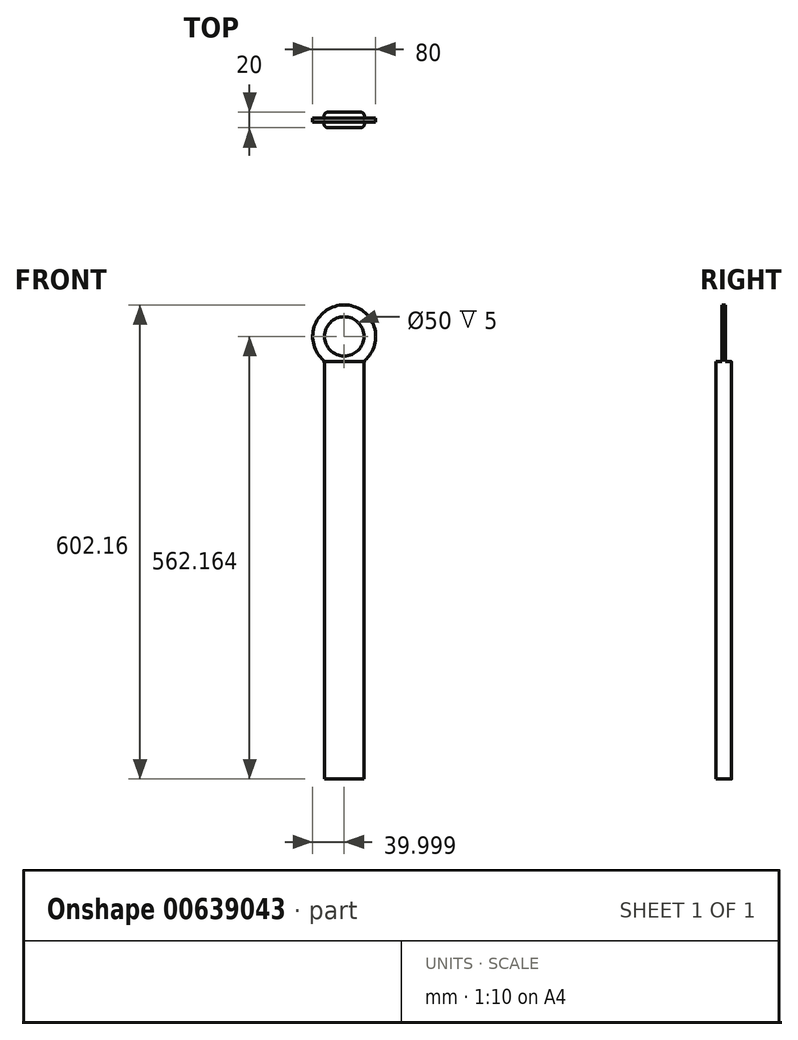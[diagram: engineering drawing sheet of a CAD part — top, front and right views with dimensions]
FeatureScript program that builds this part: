
annotation { "Feature Type Name" : "Feature", "Feature Type Description" : "" }
export const myFeature = defineFeature(function(context is Context, id is Id, definition is map)
    precondition{}
    {
        {
            var Q0;
            Q0=qCreatedBy(makeId("Front.planeOp"),FACE);
            var sketch = newSketch(context, id + "F0", { "sketchPlane" : qUnion([Q0])});
            skLineSegment(sketch, "E0", {"start": v(-85.5, -86.41) * mm, "end": v(-25.2, -86.41) * mm, "construction": true});
            skLineSegment(sketch, "E1", {"start": v(-0.2, -86.41) * mm, "end": v(-0.2, 435.75) * mm, "construction": true});
            skLineSegment(sketch, "E2", {"start": v(-25.2, -86.41) * mm, "end": v(-25.2, 440.05) * mm});
            skLineSegment(sketch, "E3", {"start": v(24.8, -86.41) * mm, "end": v(24.8, 440.05) * mm});
            skArc(sketch, "E4", {"start": v(27.8, 447.19) * mm, "mid": v(-0.2, 515.75) * mm, "end": v(-28.2, 447.19) * mm});
            skLineSegment(sketch, "E5.trimOffspring", {"start": v(24.8, -86.41) * mm, "end": v(85.11, -86.41) * mm, "construction": true});
            skLineSegment(sketch, "E6", {"start": v(-25.2, -86.41) * mm, "end": v(24.8, -86.41) * mm});
            skPoint(sketch, "E7.visualSharp", {"position": v(-25.2, 444.53) * mm});
            skArc(sketch, "E7.filletArc", {"start": v(-25.2, 440.05) * mm, "mid": v(-25.97, 443.92) * mm, "end": v(-28.2, 447.19) * mm});
            skPoint(sketch, "E8.visualSharp", {"position": v(24.8, 444.53) * mm});
            skArc(sketch, "E8.filletArc", {"start": v(27.8, 447.19) * mm, "mid": v(25.59, 443.92) * mm, "end": v(24.8, 440.05) * mm});
            skCircle(sketch, "E9", {"center": v(-0.2, 475.75) * mm, "radius": 25 * mm});
            skSolve(sketch);
        }
        {
            var Q0;
            Q0=makeQuery(id+"F0.imprint","IMPRINT",FACE,{"disambiguationData":[TD([[makeQuery(id+"F0.imprint","IMPRINT",EDGE,{"derivedFrom":sQuery(id+"F0.wireOp",EDGE,"E2")}),-1.0]])]});
            extrude(context, id + "F1", {"entities" : qUnion([Q0]), "depth" : 20 * mm, "offsetDistance" : 25 * mm});
        }
        {
            var Q0;
            Q0=makeQuery(id+"F1.opExtrude","SWEPT_FACE",FACE,{"disambiguationData":[OSD([sQuery(id+"F0.wireOp",EDGE,"E2")])]});
            var sketch = newSketch(context, id + "F2", { "sketchPlane" : qUnion([Q0])});
            skLineSegment(sketch, "E10.0", {"start": v(20, 500.75) * mm, "end": v(20, 450.75) * mm});
            skLineSegment(sketch, "E11.0", {"start": v(0, 500.75) * mm, "end": v(0, 450.75) * mm});
            skLineSegment(sketch, "E12.0", {"start": v(0, 447.19) * mm, "end": v(0, 515.75) * mm});
            skLineSegment(sketch, "E13.0", {"start": v(20, 447.19) * mm, "end": v(20, 515.75) * mm});
            skLineSegment(sketch, "E14", {"start": v(0, 515.75) * mm, "end": v(20, 515.75) * mm});
            skLineSegment(sketch, "E15", {"start": v(10, 515.75) * mm, "end": v(10, 450.75) * mm, "construction": true});
            skLineSegment(sketch, "E16", {"start": v(7.5, 443.62) * mm, "end": v(7.5, 515.75) * mm});
            skLineSegment(sketch, "E17", {"start": v(12.5, 515.75) * mm, "end": v(12.5, 443.62) * mm});
            skLineSegment(sketch, "E18.0", {"start": v(0, 440.05) * mm, "end": v(0, 447.19) * mm});
            skLineSegment(sketch, "E19.0", {"start": v(20, 440.05) * mm, "end": v(20, 447.19) * mm});
            skLineSegment(sketch, "E20", {"start": v(0, 443.62) * mm, "end": v(20, 443.62) * mm});
            skPoint(sketch, "E21.0.start.orphan", {"position": v(20, 447.19) * mm});
            skPoint(sketch, "E22.trimOffspring.end.orphan", {"position": v(0, 447.19) * mm});
            skSolve(sketch);
        }
        {
            var Q0;
            Q0=makeQuery(id+"F1.opExtrude","CAP_EDGE",EDGE,{"disambiguationData":[OSD([sQuery(id+"F0.wireOp",EDGE,"E2")])],"isStart":false});
            var Q1;
            Q1=makeQuery(id+"F1.opExtrude","CAP_EDGE",EDGE,{"disambiguationData":[OSD([sQuery(id+"F0.wireOp",EDGE,"E2")])],"isStart":true});
            fillet(context, id + "F3", {"entities" : qUnion([Q0, Q1]), "radius" : 5 * mm, "tangentPropagation" : true, "allowEdgeOverflow" : false});
        }
        {
            var Q0;
            {var subQ7=sQuery(id+"F2.wireOp",EDGE,"E16");Q0=makeQuery(id+"F2.imprint","IMPRINT",FACE,{"disambiguationData":[TD([[makeQuery(id+"F2.imprint","IMPRINT",EDGE,{"derivedFrom":subQ7}),1.0]])]});}
            var Q1;
            {var subQ7=sQuery(id+"F2.wireOp",EDGE,"E17");Q1=makeQuery(id+"F2.imprint","IMPRINT",FACE,{"disambiguationData":[TD([[makeQuery(id+"F2.imprint","IMPRINT",EDGE,{"derivedFrom":subQ7}),1.0]])]});}
            extrude(context, id + "F4", {"entities" : qUnion([Q0, Q1]), "operationType" : NewBodyOperationType.REMOVE, "endBound" : BoundingType.SYMMETRIC, "oppositeDirection" : true, "depth" : 140 * mm, "offsetDistance" : 25 * mm});
        }
    });
